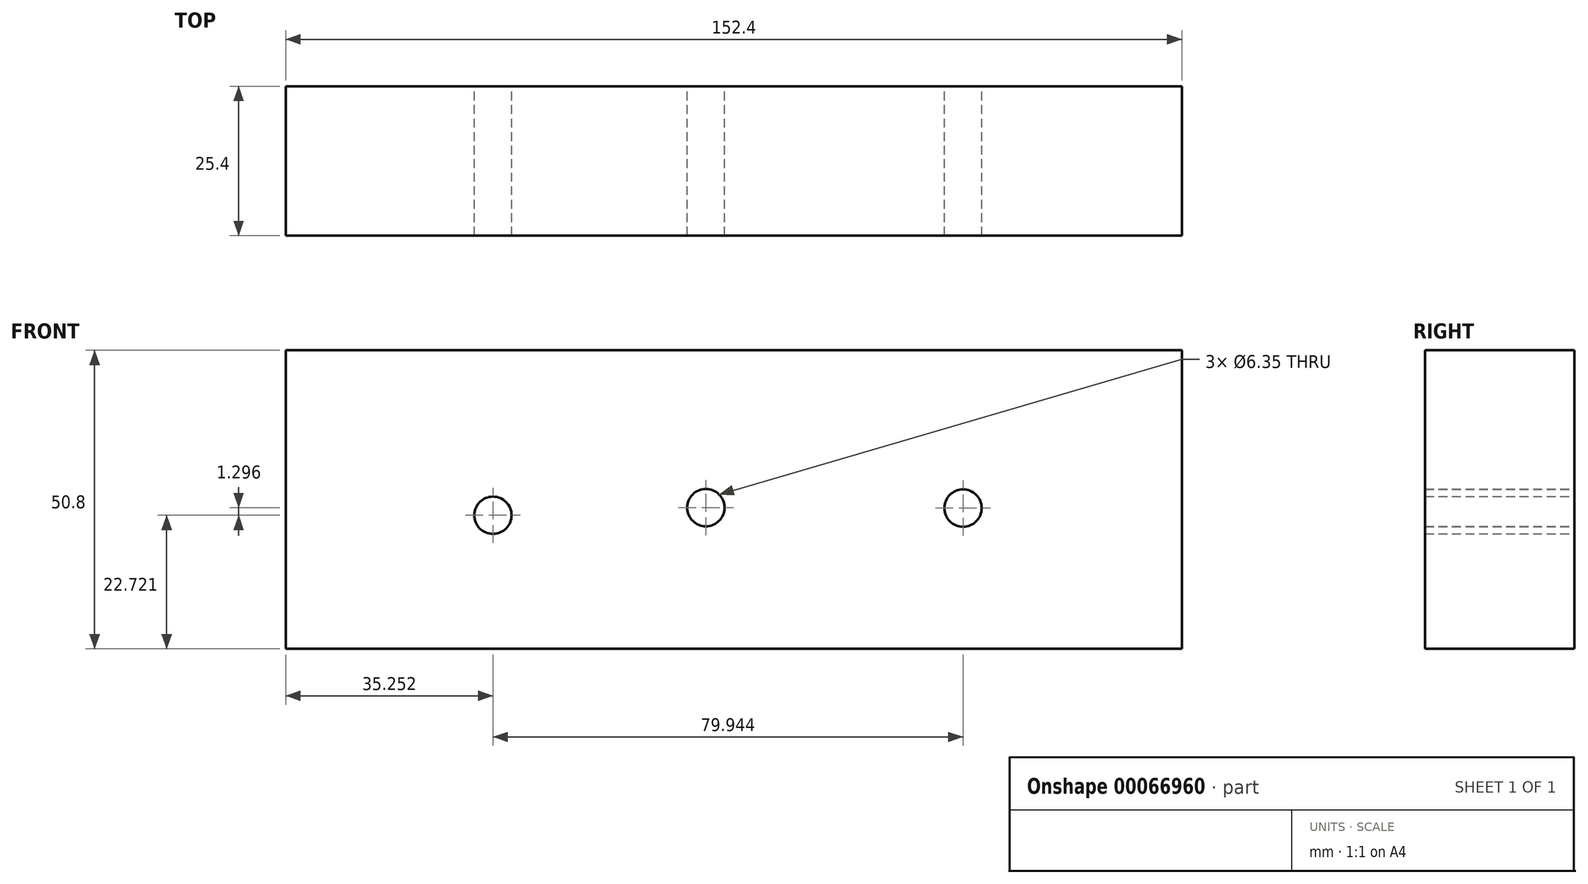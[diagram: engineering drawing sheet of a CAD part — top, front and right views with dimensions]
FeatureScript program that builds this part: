
annotation { "Feature Type Name" : "Feature", "Feature Type Description" : "" }
export const myFeature = defineFeature(function(context is Context, id is Id, definition is map)
    precondition{}
    {
        {
            var Q0;
            Q0=qCreatedBy(makeId("Front.planeOp"),FACE);
            var sketch = newSketch(context, id + "F0", { "sketchPlane" : qUnion([Q0])});
            skLineSegment(sketch, "E0.bottom", {"start": v(-46.9, 50.8) * mm, "end": v(105.5, 50.8) * mm});
            skLineSegment(sketch, "E0.top", {"start": v(-46.9, 0) * mm, "end": v(105.5, 0) * mm});
            skLineSegment(sketch, "E0.left", {"start": v(-46.9, 50.8) * mm, "end": v(-46.9, 0) * mm});
            skLineSegment(sketch, "E0.right", {"start": v(105.5, 50.8) * mm, "end": v(105.5, 0) * mm});
            skLineSegment(sketch, "E1.bottom", {"start": v(34.22, 50.8) * mm, "end": v(31.64, 50.8) * mm});
            skLineSegment(sketch, "E1.top", {"start": v(34.22, 0) * mm, "end": v(31.64, 0) * mm});
            skPoint(sketch, "E2", {"position": v(-11.64, 22.72) * mm});
            skPoint(sketch, "E3", {"position": v(24.58, 24.02) * mm});
            skPoint(sketch, "E4", {"position": v(68.3, 23.94) * mm});
            skSolve(sketch);
        }
        {
            var Q0;
            {var subQ3=sQuery(id+"F0.wireOp",EDGE,"E0.left");Q0=makeQuery(id+"F0.imprint","IMPRINT",FACE,{"disambiguationData":[TD([[makeQuery(id+"F0.imprint","IMPRINT",EDGE,{"derivedFrom":subQ3}),1.0]])]});}
            extrude(context, id + "F1", {"entities" : qUnion([Q0]), "depth" : 25.4 * mm});
        }
        {
            var Q0;
            Q0=sQuery(id+"F0.wireOp",VERTEX,"E3");
            var Q1;
            Q1=sQuery(id+"F0.wireOp",VERTEX,"E2");
            var Q2;
            Q2=sQuery(id+"F0.wireOp",VERTEX,"E4");
            var Q3;
            Q3=makeQuery(id+"F1.opExtrude","SWEPT_BODY",BODY,{"disambiguationData":[OSD([sQuery(id+"F0.wireOp",EDGE,"E0.bottom"),sQuery(id+"F0.wireOp",EDGE,"E0.top"),sQuery(id+"F0.wireOp",EDGE,"E0.left"),sQuery(id+"F0.wireOp",EDGE,"E0.right"),sQuery(id+"F0.wireOp",EDGE,"E1.bottom"),sQuery(id+"F0.wireOp",EDGE,"E1.top")])]});
            hole(context, id + "F2", {"style" : HoleStyle.SIMPLE, "holeDiameter" : 6.35 * mm, "endStyle" : HoleEndStyle.THROUGH, "oppositeDirection" : true, "locations" : qUnion([Q0, Q1, Q2]), "scope" : qUnion([Q3])});
        }
    });
